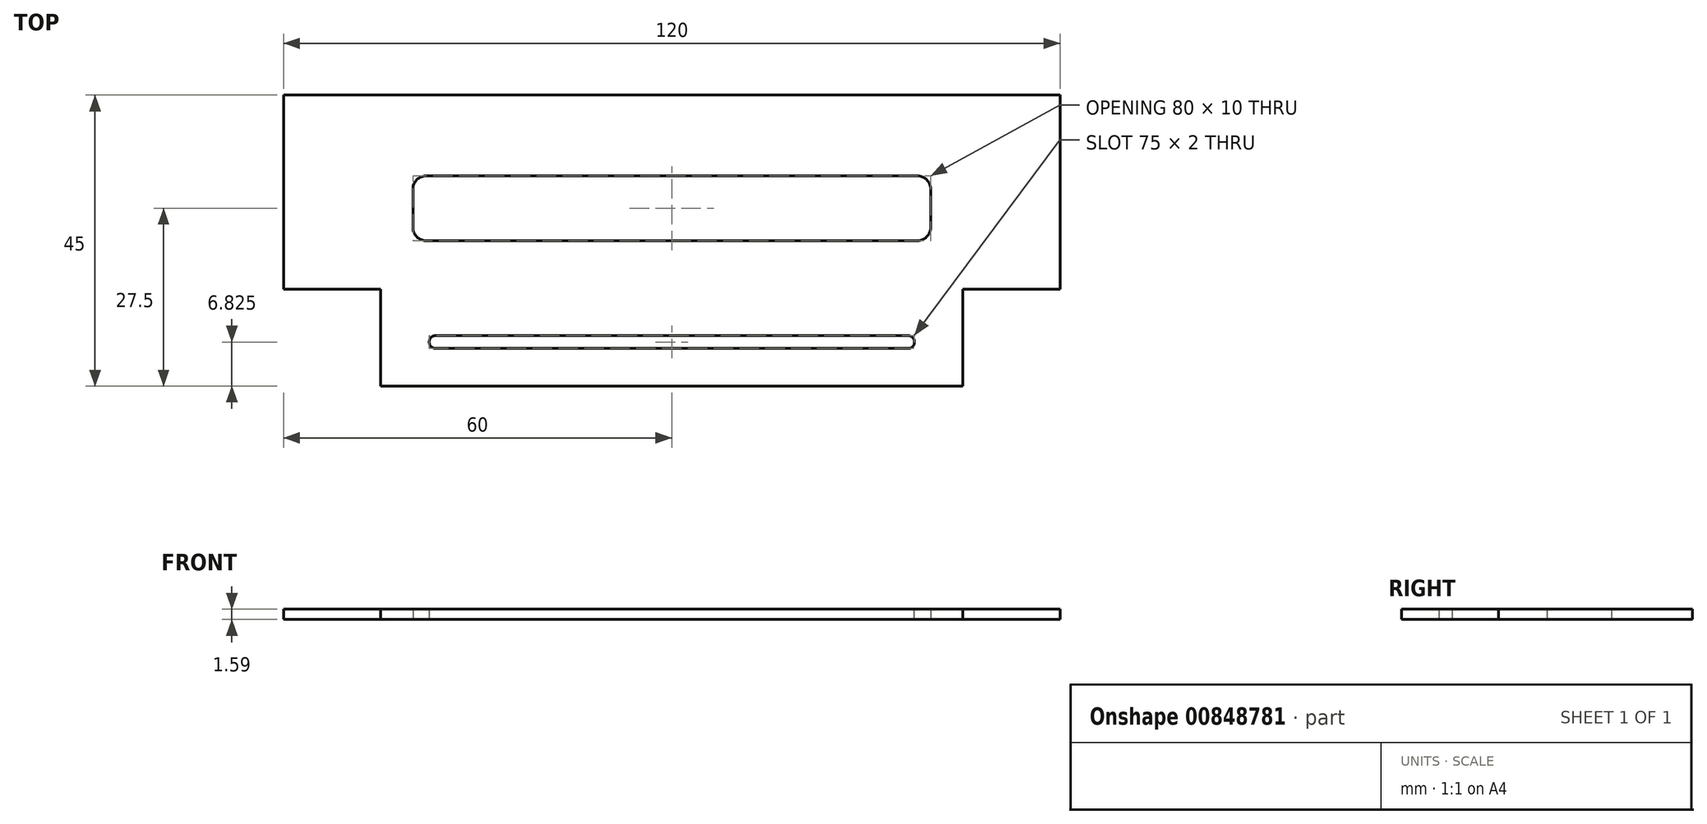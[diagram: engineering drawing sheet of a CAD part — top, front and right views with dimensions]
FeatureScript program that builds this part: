
annotation { "Feature Type Name" : "Feature", "Feature Type Description" : "" }
export const myFeature = defineFeature(function(context is Context, id is Id, definition is map)
    precondition{}
    {
        {
            var Q0;
            Q0=qCreatedBy(makeId("Top.planeOp"),FACE);
            var sketch = newSketch(context, id + "F0", { "sketchPlane" : qUnion([Q0])});
            skLineSegment(sketch, "E0.bottom", {"start": v(-45, 0) * mm, "end": v(45, 0) * mm});
            skLineSegment(sketch, "E0.top", {"start": v(-45, -45) * mm, "end": v(45, -45) * mm});
            skLineSegment(sketch, "E0.left", {"start": v(-45, -30) * mm, "end": v(-45, -45) * mm});
            skLineSegment(sketch, "E0.right", {"start": v(45, -30) * mm, "end": v(45, -45) * mm});
            skLineSegment(sketch, "E1.bottom", {"start": v(-40, -12.5) * mm, "end": v(40, -12.5) * mm});
            skLineSegment(sketch, "E1.top", {"start": v(-40, -22.5) * mm, "end": v(40, -22.5) * mm});
            skLineSegment(sketch, "E1.left", {"start": v(-40, -12.5) * mm, "end": v(-40, -22.5) * mm});
            skLineSegment(sketch, "E1.right", {"start": v(40, -12.5) * mm, "end": v(40, -22.5) * mm});
            skLineSegment(sketch, "E2.bottom", {"start": v(-37.5, -37.18) * mm, "end": v(37.5, -37.17) * mm});
            skLineSegment(sketch, "E2.top", {"start": v(-37.5, -39.18) * mm, "end": v(37.5, -39.17) * mm});
            skLineSegment(sketch, "E2.left", {"start": v(-37.5, -37.18) * mm, "end": v(-37.5, -39.18) * mm});
            skLineSegment(sketch, "E2.right", {"start": v(37.5, -37.17) * mm, "end": v(37.5, -39.17) * mm});
            skLineSegment(sketch, "E3.bottom", {"start": v(-45, 0) * mm, "end": v(-60, 0) * mm});
            skLineSegment(sketch, "E3.top", {"start": v(-45, -30) * mm, "end": v(-60, -30) * mm});
            skLineSegment(sketch, "E3.right", {"start": v(-60, 0) * mm, "end": v(-60, -30) * mm});
            skLineSegment(sketch, "E4.bottom", {"start": v(45, 0) * mm, "end": v(60, 0) * mm});
            skLineSegment(sketch, "E4.top", {"start": v(45, -30) * mm, "end": v(60, -30) * mm});
            skLineSegment(sketch, "E4.right", {"start": v(60, 0) * mm, "end": v(60, -30) * mm});
            skSolve(sketch);
        }
        {
            var Q0;
            Q0 = qSketchRegion(id + "F0", true);
            extrude(context, id + "F1", {"entities" : qUnion([Q0]), "depth" : 1.59 * mm, "offsetDistance" : 25 * mm});
        }
        {
            var Q0;
            Q0=makeQuery(id+"F1.opExtrude","SWEPT_EDGE",EDGE,{"disambiguationData":[OSD([sQuery(id+"F0.wireOp",EDGE,"E1.top"),sQuery(id+"F0.wireOp",EDGE,"E1.right")])]});
            var Q1;
            Q1=makeQuery(id+"F1.opExtrude","SWEPT_EDGE",EDGE,{"disambiguationData":[OSD([sQuery(id+"F0.wireOp",EDGE,"E1.bottom"),sQuery(id+"F0.wireOp",EDGE,"E1.left")])]});
            var Q2;
            Q2=makeQuery(id+"F1.opExtrude","SWEPT_EDGE",EDGE,{"disambiguationData":[OSD([sQuery(id+"F0.wireOp",EDGE,"E1.bottom"),sQuery(id+"F0.wireOp",EDGE,"E1.right")])]});
            var Q3;
            Q3=makeQuery(id+"F1.opExtrude","SWEPT_EDGE",EDGE,{"disambiguationData":[OSD([sQuery(id+"F0.wireOp",EDGE,"E1.top"),sQuery(id+"F0.wireOp",EDGE,"E1.left")])]});
            fillet(context, id + "F2", {"entities" : qUnion([Q0, Q1, Q2, Q3]), "radius" : 2 * mm, "tangentPropagation" : true, "allowEdgeOverflow" : false});
        }
        {
            var Q0;
            Q0=makeQuery(id+"F1.opExtrude","SWEPT_EDGE",EDGE,{"disambiguationData":[OSD([sQuery(id+"F0.wireOp",EDGE,"E2.bottom"),sQuery(id+"F0.wireOp",EDGE,"E2.left")])]});
            var Q1;
            Q1=makeQuery(id+"F1.opExtrude","SWEPT_EDGE",EDGE,{"disambiguationData":[OSD([sQuery(id+"F0.wireOp",EDGE,"E2.bottom"),sQuery(id+"F0.wireOp",EDGE,"E2.right")])]});
            var Q2;
            Q2=makeQuery(id+"F1.opExtrude","SWEPT_EDGE",EDGE,{"disambiguationData":[OSD([sQuery(id+"F0.wireOp",EDGE,"E2.top"),sQuery(id+"F0.wireOp",EDGE,"E2.right")])]});
            var Q3;
            Q3=makeQuery(id+"F1.opExtrude","SWEPT_EDGE",EDGE,{"disambiguationData":[OSD([sQuery(id+"F0.wireOp",EDGE,"E2.top"),sQuery(id+"F0.wireOp",EDGE,"E2.left")])]});
            fillet(context, id + "F3", {"entities" : qUnion([Q0, Q1, Q2, Q3]), "radius" : 1 * mm, "tangentPropagation" : true, "allowEdgeOverflow" : false});
        }
    });
